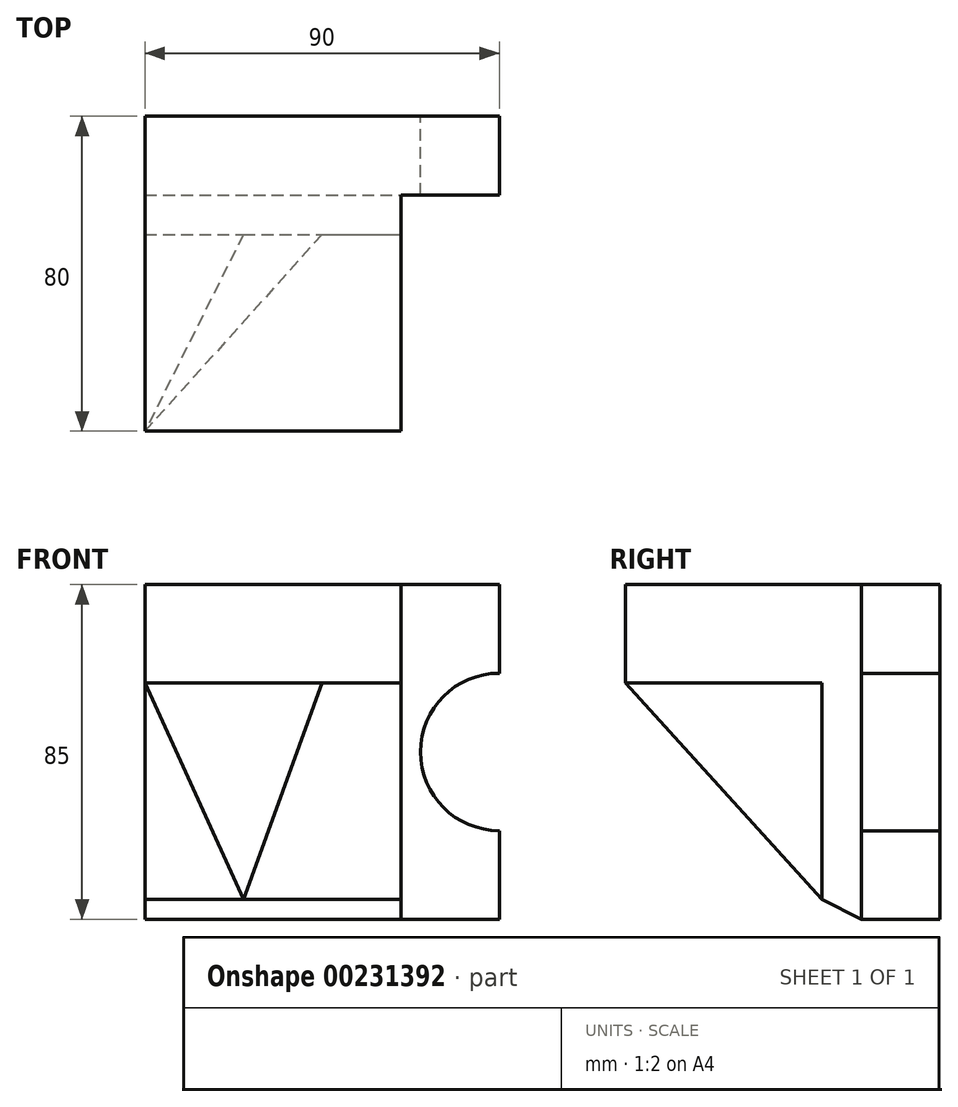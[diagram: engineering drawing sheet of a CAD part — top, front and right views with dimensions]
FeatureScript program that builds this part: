
annotation { "Feature Type Name" : "Feature", "Feature Type Description" : "" }
export const myFeature = defineFeature(function(context is Context, id is Id, definition is map)
    precondition{}
    {
        {
            var Q0;
            Q0=qCreatedBy(makeId("Front.planeOp"),FACE);
            var sketch = newSketch(context, id + "F0", { "sketchPlane" : qUnion([Q0])});
            skLineSegment(sketch, "E0.bottom", {"start": v(45, 42.5) * mm, "end": v(-45, 42.5) * mm});
            skLineSegment(sketch, "E0.top", {"start": v(45, -42.5) * mm, "end": v(-45, -42.5) * mm});
            skLineSegment(sketch, "E0.left", {"start": v(45, 42.5) * mm, "end": v(45, -42.5) * mm});
            skLineSegment(sketch, "E0.right", {"start": v(-45, 42.5) * mm, "end": v(-45, -42.5) * mm});
            skPoint(sketch, "E0.middle", {"position": v(0, 0) * mm});
            skSolve(sketch);
        }
        {
            var Q0;
            Q0=qSketchRegion(id+"F0",true);
            extrude(context, id + "F1", {"entities" : qUnion([Q0]), "depth" : 20 * mm});
        }
        {
            var Q0;
            Q0=qCreatedBy(makeId("Front.planeOp"),FACE);
            var sketch = newSketch(context, id + "F2", { "sketchPlane" : qUnion([Q0])});
            skArc(sketch, "E1", {"start": v(45, 20) * mm, "mid": v(25, 0) * mm, "end": v(45, -20) * mm});
            skLineSegment(sketch, "E2.0", {"start": v(45, 42.5) * mm, "end": v(45, -42.5) * mm});
            skSolve(sketch);
        }
        {
            var Q0;
            {var subQ0=sQuery(id+"F2.wireOp",EDGE,"E1");Q0=makeQuery(id+"F2.imprint","IMPRINT",FACE,{"disambiguationData":[TD([[makeQuery(id+"F2.imprint","IMPRINT",EDGE,{"derivedFrom":subQ0}),1.0]])]});}
            extrude(context, id + "F3", {"entities" : qUnion([Q0]), "operationType" : NewBodyOperationType.REMOVE, "depth" : 25 * mm});
        }
        {
            var Q0;
            {var subQ0=sQuery(id+"F0.wireOp",EDGE,"E0.bottom");var subQ2=sQuery(id+"F0.wireOp",EDGE,"E0.left");Q0=makeQuery(id+"F3.boolean.opBoolean","SPLIT",FACE,{"disambiguationData":[TD([makeQuery(id+"F1.opExtrude","SWEPT_FACE",FACE,{"disambiguationData":[OSD([subQ0])]})])],"derivedFrom":makeQuery(id+"F1.opExtrude","SWEPT_FACE",FACE,{"disambiguationData":[OSD([subQ2])]})});}
            cPlane(context, id + "F4", {"entities" : qUnion([Q0]), "cplaneType" : CPlaneType.OFFSET, "offset" : 25 * mm, "oppositeDirection" : true, "width" : 150 * mm, "height" : 150 * mm});
        }
        {
            var Q0;
            Q0=qCreatedBy(id+"F4.planeOp",FACE);
            var sketch = newSketch(context, id + "F5", { "sketchPlane" : qUnion([Q0])});
            skLineSegment(sketch, "E3", {"start": v(-20, 42.5) * mm, "end": v(-80, 42.5) * mm});
            skLineSegment(sketch, "E4", {"start": v(-80, 42.5) * mm, "end": v(-80, 17.5) * mm});
            skLineSegment(sketch, "E5", {"start": v(-80, 17.5) * mm, "end": v(-30, 17.5) * mm});
            skLineSegment(sketch, "E6", {"start": v(-30, 17.5) * mm, "end": v(-30, -37.5) * mm});
            skLineSegment(sketch, "E7", {"start": v(-30, -37.5) * mm, "end": v(-20, -42.5) * mm});
            skPoint(sketch, "E8.0", {"position": v(-20, -31.25) * mm});
            skLineSegment(sketch, "E9.0", {"start": v(-20, 20) * mm, "end": v(-20, -20) * mm});
            skLineSegment(sketch, "E10.0.0", {"start": v(-20, 42.5) * mm, "end": v(-20, 20) * mm});
            skLineSegment(sketch, "E10.0.1", {"start": v(-20, 20) * mm, "end": v(0, 20) * mm});
            skLineSegment(sketch, "E10.0.2", {"start": v(0, 20) * mm, "end": v(0, 42.5) * mm});
            skLineSegment(sketch, "E10.0.3", {"start": v(0, 42.5) * mm, "end": v(-20, 42.5) * mm});
            skLineSegment(sketch, "E11", {"start": v(-20, -42.5) * mm, "end": v(-20, 42.5) * mm});
            skSolve(sketch);
        }
        {
            var Q0;
            {var subQ1=sQuery(id+"F5.wireOp",EDGE,"E3");Q0=makeQuery(id+"F5.imprint","IMPRINT",FACE,{"disambiguationData":[TD([[makeQuery(id+"F5.imprint","IMPRINT",EDGE,{"derivedFrom":subQ1}),1.0]])]});}
            extrude(context, id + "F6", {"entities" : qUnion([Q0]), "operationType" : NewBodyOperationType.ADD, "oppositeDirection" : true, "depth" : 65 * mm});
        }
        {
            var Q0;
            Q0=makeQuery(id+"F6.opExtrude","SWEPT_FACE",FACE,{"disambiguationData":[OSD([sQuery(id+"F5.wireOp",EDGE,"E6")])]});
            var sketch = newSketch(context, id + "F7", { "sketchPlane" : qUnion([Q0])});
            skPoint(sketch, "E12", {"position": v(0, 17.5) * mm});
            skPoint(sketch, "E13", {"position": v(-20, -37.5) * mm});
            skSolve(sketch);
        }
        {
            var Q0;
            {var subQ0=sQuery(id+"F5.wireOp",EDGE,"E6");Q0=makeQuery(id+"F7.imprint","IMPRINT",FACE,{"disambiguationData":[TD([[makeQuery(id+"F7.imprint","IMPRINT",EDGE,{"derivedFrom":makeQuery(id+"F6.opExtrude","CAP_EDGE",EDGE,{"disambiguationData":[OSD([subQ0])],"isStart":true})}),-1.0]])]});}
            var sketch = newSketch(context, id + "F8", { "sketchPlane" : qUnion([Q0])});
            skLineSegment(sketch, "E14", {"start": v(-20, -37.5) * mm, "end": v(0, 17.5) * mm});
            skLineSegment(sketch, "E15.0", {"start": v(-45, -37.5) * mm, "end": v(-20, -37.5) * mm});
            skPoint(sketch, "E16.orphan", {"position": v(20, -37.5) * mm});
            skLineSegment(sketch, "E17.0", {"start": v(-45, 17.5) * mm, "end": v(-45, -37.5) * mm});
            skLineSegment(sketch, "E18.0", {"start": v(-45, 17.5) * mm, "end": v(0, 17.5) * mm});
            skPoint(sketch, "E19.orphan", {"position": v(20, 17.5) * mm});
            skSolve(sketch);
        }
        {
            var Q0;
            Q0=makeQuery(id+"F6.opExtrude","SWEPT_FACE",FACE,{"disambiguationData":[OSD([sQuery(id+"F5.wireOp",EDGE,"E4")])]});
            var sketch = newSketch(context, id + "F9", { "sketchPlane" : qUnion([Q0])});
            skPoint(sketch, "E20", {"position": v(-45, 17.5) * mm});
            skSolve(sketch);
        }
        {
            var Q1;
            Q1=makeQuery(id+"F8.imprint","IMPRINT",FACE,{"disambiguationData":[TD([[makeQuery(id+"F8.imprint","IMPRINT",EDGE,{"derivedFrom":sQuery(id+"F8.wireOp",EDGE,"E14")}),1.0]])]});
            var Q2;
            Q2=sQuery(id+"F9.wireOp",VERTEX,"E20");
            loft(context, id + "F10", {"operationType" : NewBodyOperationType.ADD, "sheetProfilesArray" : [{ "sheetProfileEntities" : qUnion([Q1]) }, { "sheetProfileEntities" : qUnion([Q2]) }]});
        }
    });
